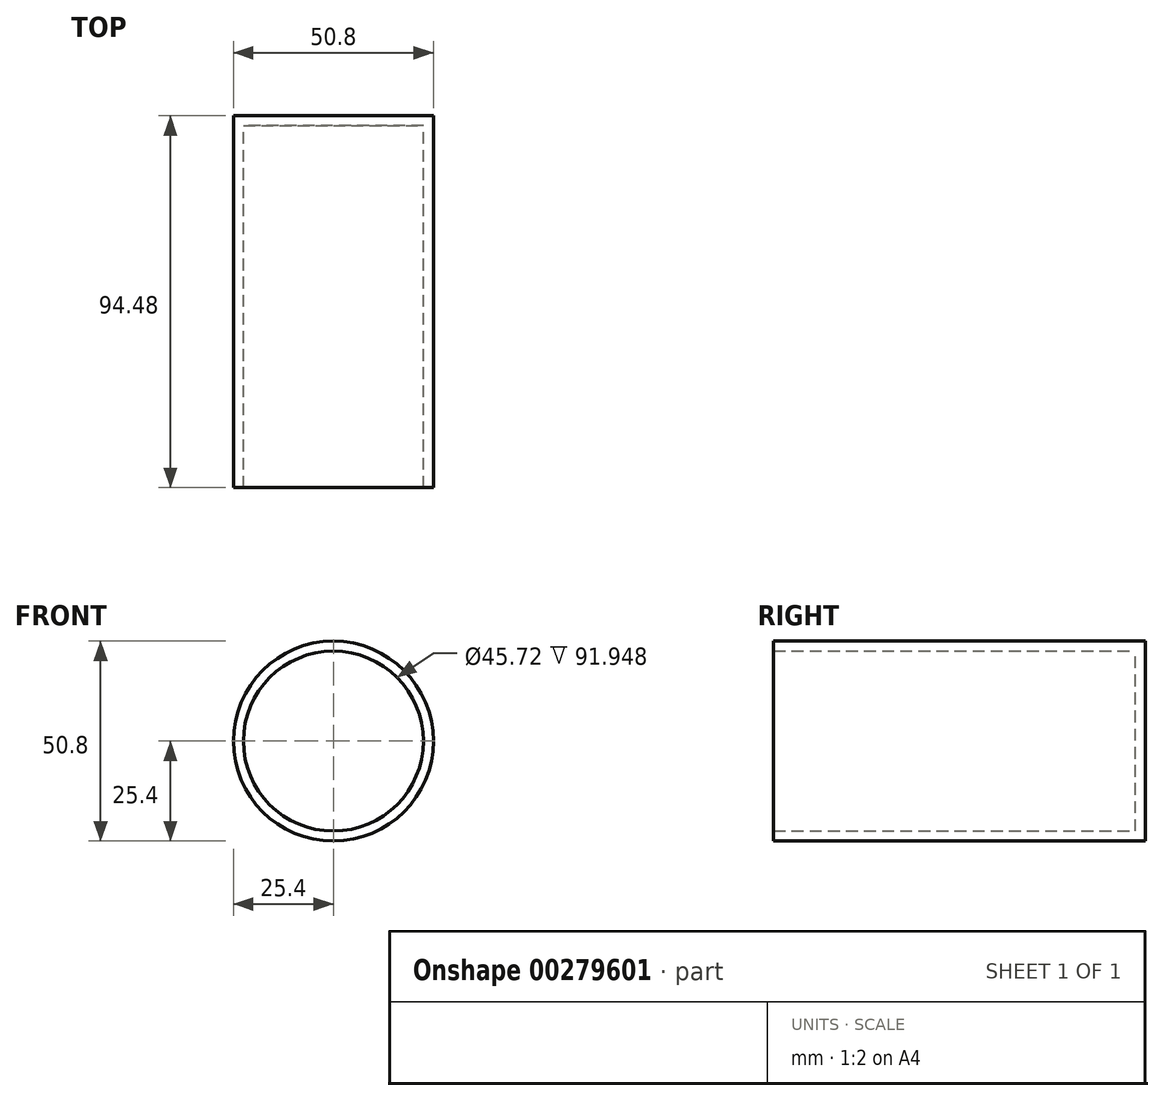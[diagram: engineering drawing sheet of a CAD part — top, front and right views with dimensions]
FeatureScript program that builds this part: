
annotation { "Feature Type Name" : "Feature", "Feature Type Description" : "" }
export const myFeature = defineFeature(function(context is Context, id is Id, definition is map)
    precondition{}
    {
        {
            var Q0;
            Q0=qCreatedBy(makeId("Front.planeOp"),FACE);
            var sketch = newSketch(context, id + "F0", { "sketchPlane" : qUnion([Q0])});
            skCircle(sketch, "E0", {"center": v(0, 0) * mm, "radius": 25.4 * mm});
            skSolve(sketch);
        }
        {
            var Q0;
            Q0=makeQuery(id+"F0.imprint","IMPRINT",FACE,{"disambiguationData":[TD([[makeQuery(id+"F0.imprint","IMPRINT",EDGE,{"derivedFrom":sQuery(id+"F0.wireOp",EDGE,"E0")}),1.0]])]});
            extrude(context, id + "F1", {"entities" : qUnion([Q0]), "endBound" : BoundingType.SYMMETRIC, "depth" : 94.49 * mm});
        }
        {
            var Q0;
            Q0=makeQuery(id+"F1.opExtrude","CAP_FACE",FACE,{"disambiguationData":[OSD([sQuery(id+"F0.wireOp",EDGE,"E0")])],"isStart":false});
            shell(context, id + "F2", {"entities" : qUnion([Q0]), "thickness" : 2.54 * mm});
        }
    });
